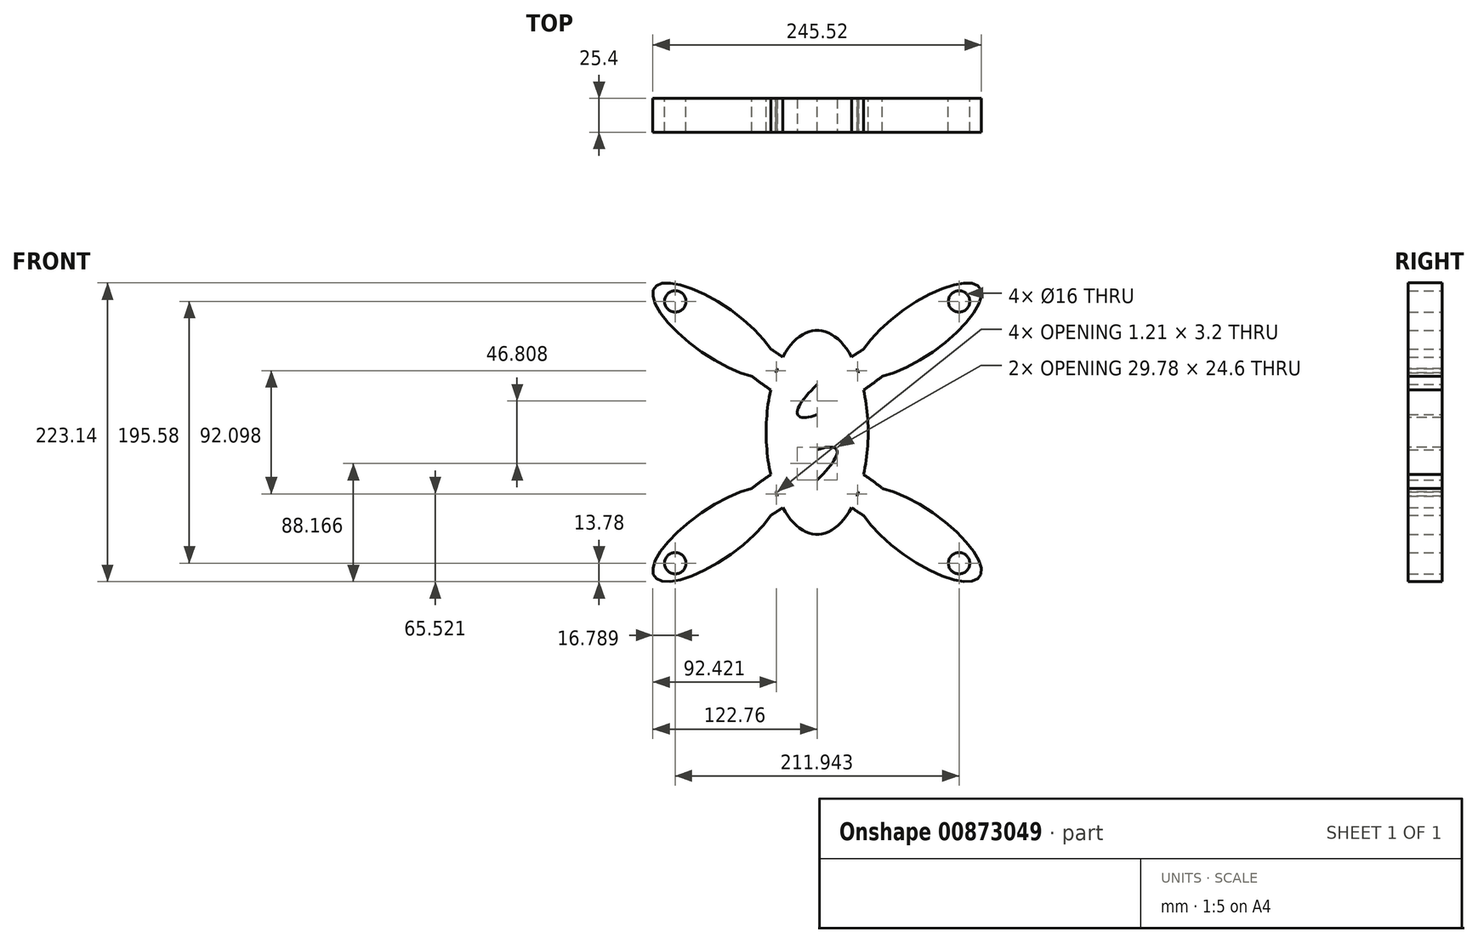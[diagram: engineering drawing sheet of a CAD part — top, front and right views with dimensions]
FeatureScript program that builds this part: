
annotation { "Feature Type Name" : "Feature", "Feature Type Description" : "" }
export const myFeature = defineFeature(function(context is Context, id is Id, definition is map)
    precondition{}
    {
        {
            var Q0;
            Q0=qCreatedBy(makeId("Front.planeOp"),FACE);
            var sketch = newSketch(context, id + "F0", { "sketchPlane" : qUnion([Q0])});
            skEllipse(sketch, "E0", {"center": v(0, 0) * mm, "majorRadius": 76.2 * mm, "minorRadius": 38.1 * mm, "majorAxis": v(0, 1)});
            skPoint(sketch, "E1", {"position": v(76.2, 0) * mm});
            skPoint(sketch, "E2", {"position": v(76.2, 76.2) * mm});
            skPoint(sketch, "E3", {"position": v(30.95, 44.45) * mm});
            skPoint(sketch, "E4", {"position": v(38.1, 0) * mm});
            skPoint(sketch, "E5", {"position": v(-38.1, 0) * mm});
            skPoint(sketch, "E6", {"position": v(0, 76.2) * mm});
            skPoint(sketch, "E7", {"position": v(-30.95, 44.45) * mm});
            skPoint(sketch, "E8", {"position": v(0, -76.2) * mm});
            skPoint(sketch, "E9", {"position": v(-30.95, -44.45) * mm});
            skPoint(sketch, "E10", {"position": v(30.95, -44.45) * mm});
            skPoint(sketch, "E11", {"position": v(76.2, -76.2) * mm});
            skPoint(sketch, "E12", {"position": v(-76.2, -76.2) * mm});
            skPoint(sketch, "E13", {"position": v(-76.2, 76.2) * mm});
            skEllipse(sketch, "E14", {"center": v(76.2, -76.2) * mm, "majorRadius": 55.28 * mm, "minorRadius": 19.05 * mm, "majorAxis": v(-0.82, 0.57)});
            skEllipse(sketch, "E15", {"center": v(76.2, 76.2) * mm, "majorRadius": 55.28 * mm, "minorRadius": 19.05 * mm, "majorAxis": v(-0.82, -0.57)});
            skEllipse(sketch, "E16", {"center": v(-76.2, 76.2) * mm, "majorRadius": 55.28 * mm, "minorRadius": 19.05 * mm, "majorAxis": v(0.82, -0.57)});
            skEllipse(sketch, "E17", {"center": v(-76.2, -76.2) * mm, "majorRadius": 55.28 * mm, "minorRadius": 19.05 * mm, "majorAxis": v(0.82, 0.57)});
            skEllipse(sketch, "E18", {"center": v(-30.95, 44.45) * mm, "majorRadius": 55.28 * mm, "minorRadius": 12.7 * mm, "majorAxis": v(-0.82, 0.57)});
            skEllipse(sketch, "E19", {"center": v(30.95, 44.45) * mm, "majorRadius": 55.28 * mm, "minorRadius": 12.7 * mm, "majorAxis": v(0.82, 0.57)});
            skEllipse(sketch, "E20", {"center": v(30.95, -44.45) * mm, "majorRadius": 55.28 * mm, "minorRadius": 12.7 * mm, "majorAxis": v(0.82, -0.57)});
            skEllipse(sketch, "E21", {"center": v(-30.95, -44.45) * mm, "majorRadius": 55.28 * mm, "minorRadius": 12.7 * mm, "majorAxis": v(-0.82, -0.57)});
            skPoint(sketch, "E22", {"position": v(-105.97, 76.2) * mm});
            skPoint(sketch, "E23", {"position": v(105.97, 76.2) * mm});
            skPoint(sketch, "E24", {"position": v(105.97, -76.2) * mm});
            skPoint(sketch, "E25", {"position": v(-105.97, -76.2) * mm});
            skPoint(sketch, "E26", {"position": v(-105.97, 97.8) * mm});
            skPoint(sketch, "E27", {"position": v(105.97, 97.8) * mm});
            skPoint(sketch, "E28", {"position": v(105.97, -97.8) * mm});
            skPoint(sketch, "E29", {"position": v(-105.97, -97.8) * mm});
            skCircle(sketch, "E30", {"center": v(-105.97, -97.8) * mm, "radius": 8 * mm});
            skPoint(sketch, "E31", {"position": v(-97.97, -97.8) * mm});
            skCircle(sketch, "E32", {"center": v(105.97, -97.8) * mm, "radius": 8 * mm});
            skCircle(sketch, "E33", {"center": v(-105.97, 97.8) * mm, "radius": 8 * mm});
            skCircle(sketch, "E34", {"center": v(105.97, 97.8) * mm, "radius": 8 * mm});
            skPoint(sketch, "E35", {"position": v(-97.97, 97.8) * mm});
            skPoint(sketch, "E36", {"position": v(97.97, 97.8) * mm});
            skPoint(sketch, "E37", {"position": v(97.97, -97.8) * mm});
            skSolve(sketch);
        }
        {
            var Q0;
            Q0 = qSketchRegion(id + "F0", true);
            extrude(context, id + "F1", {"entities" : qUnion([Q0]), "depth" : 25.4 * mm, "offsetDistance" : 25.4 * mm});
        }
    });
